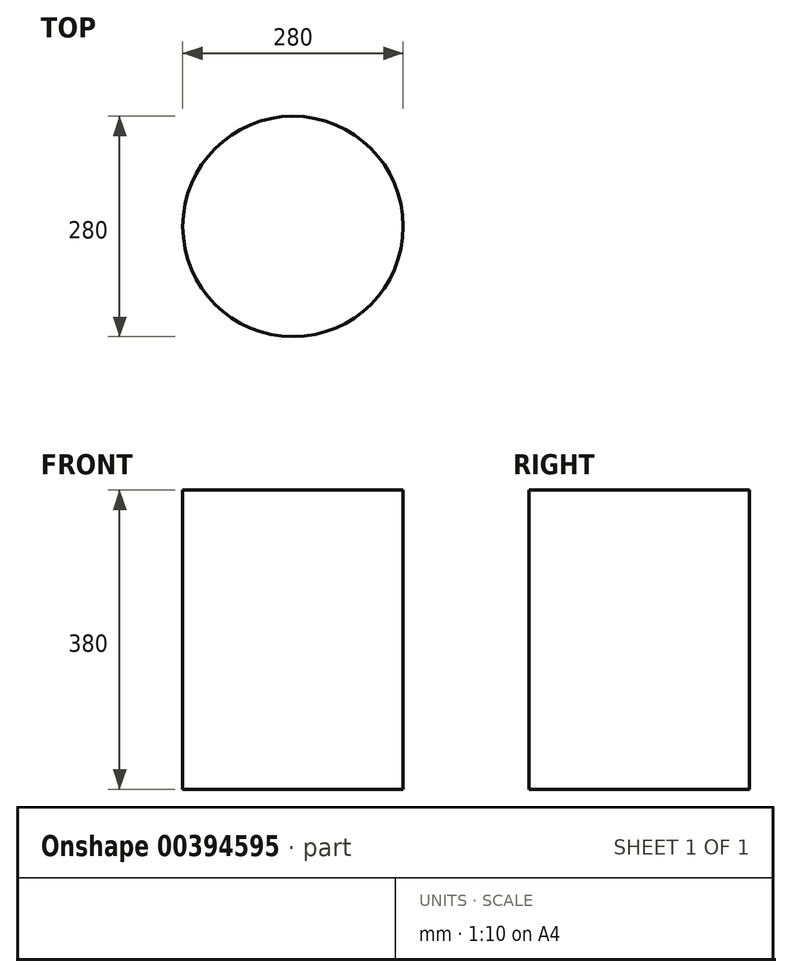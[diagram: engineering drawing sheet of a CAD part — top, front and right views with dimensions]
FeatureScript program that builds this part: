
annotation { "Feature Type Name" : "Feature", "Feature Type Description" : "" }
export const myFeature = defineFeature(function(context is Context, id is Id, definition is map)
    precondition{}
    {
        {
            var Q0;
            Q0=qCreatedBy(makeId("Top.planeOp"),FACE);
            var sketch = newSketch(context, id + "F0", { "sketchPlane" : qUnion([Q0])});
            skCircle(sketch, "E0", {"center": v(0, 0) * mm, "radius": 140 * mm});
            skSolve(sketch);
        }
        {
            var Q0;
            Q0=makeQuery(id+"F0.imprint","IMPRINT",FACE,{"disambiguationData":[TD([[makeQuery(id+"F0.imprint","IMPRINT",EDGE,{"derivedFrom":sQuery(id+"F0.wireOp",EDGE,"E0")}),1.0]])]});
            extrude(context, id + "F1", {"entities" : qUnion([Q0]), "depth" : 380 * mm});
        }
    });
